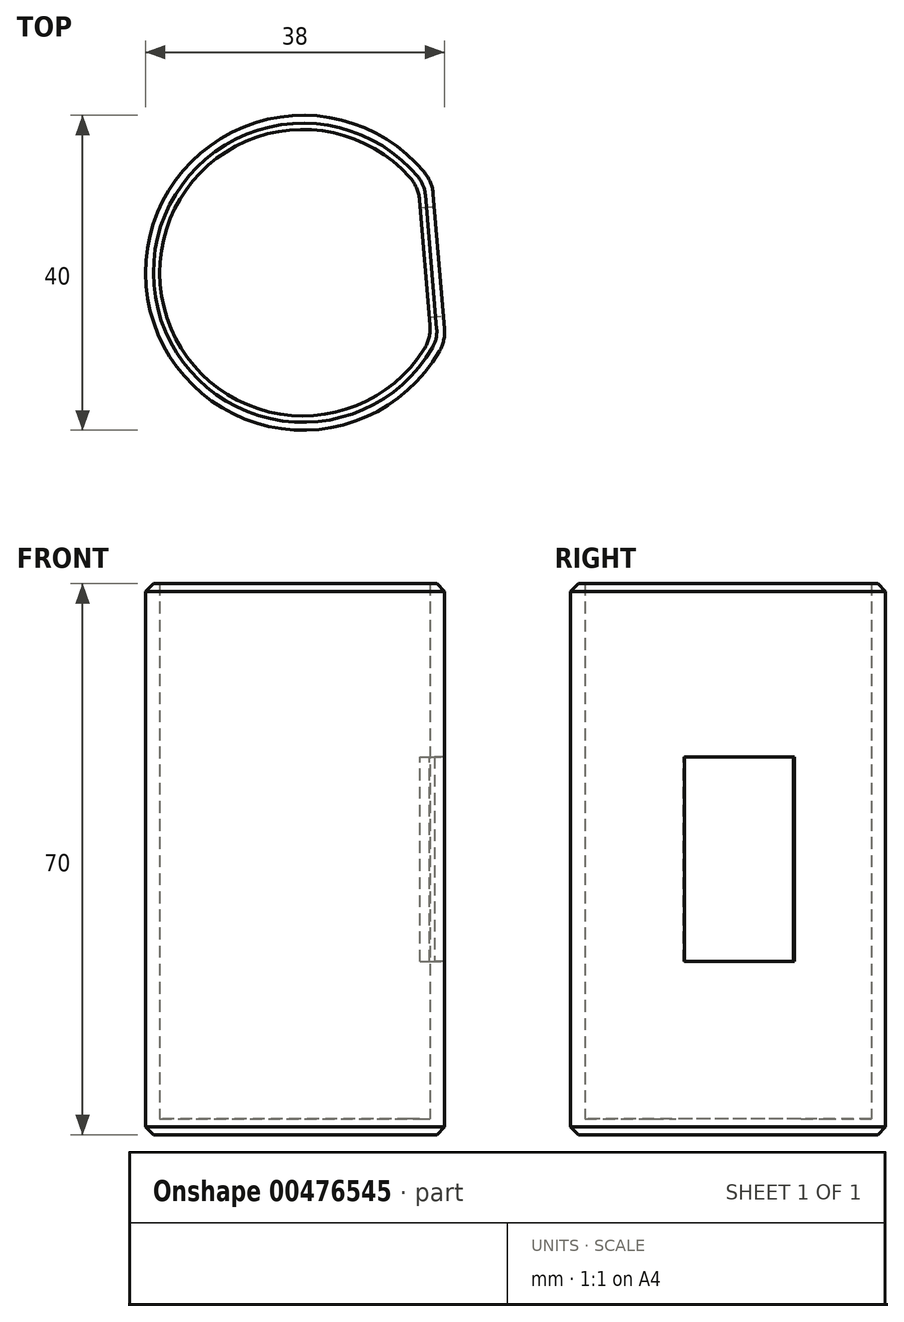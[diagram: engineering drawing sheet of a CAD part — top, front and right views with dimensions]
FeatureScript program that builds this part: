
annotation { "Feature Type Name" : "Feature", "Feature Type Description" : "" }
export const myFeature = defineFeature(function(context is Context, id is Id, definition is map)
    precondition{}
    {
        {
            var Q0;
            Q0=qCreatedBy(makeId("Top.planeOp"),FACE);
            var sketch = newSketch(context, id + "F0", { "sketchPlane" : qUnion([Q0])});
            skArc(sketch, "E0", {"start": v(16.42, 11.42) * mm, "mid": v(-19.93, -1.68) * mm, "end": v(18.1, -8.5) * mm});
            skLineSegment(sketch, "E1", {"start": v(16.42, 11.42) * mm, "end": v(18.1, -8.5) * mm});
            skArc(sketch, "E2.0", {"start": v(14.67, 10.78) * mm, "mid": v(-18.14, -1.53) * mm, "end": v(16.26, -8.17) * mm});
            skLineSegment(sketch, "E3.0", {"start": v(14.67, 10.78) * mm, "end": v(16.26, -8.17) * mm});
            skSolve(sketch);
        }
        {
            var Q0;
            Q0=makeQuery(id+"F0.imprint","IMPRINT",FACE,{"disambiguationData":[TD([[makeQuery(id+"F0.imprint","IMPRINT",EDGE,{"derivedFrom":sQuery(id+"F0.wireOp",EDGE,"E0")}),1.0]])]});
            extrude(context, id + "F1", {"entities" : qUnion([Q0]), "depth" : 70 * mm});
        }
        {
            var Q0;
            Q0=makeQuery(id+"F0.imprint","IMPRINT",FACE,{"disambiguationData":[TD([[makeQuery(id+"F0.imprint","IMPRINT",EDGE,{"derivedFrom":sQuery(id+"F0.wireOp",EDGE,"E2.0")}),1.0]])]});
            extrude(context, id + "F2", {"entities" : qUnion([Q0]), "operationType" : NewBodyOperationType.ADD, "depth" : 2 * mm});
        }
        {
            var Q0;
            {var subQ0=sQuery(id+"F0.wireOp",EDGE,"E1");var subQ1=sQuery(id+"F0.wireOp",EDGE,"E0");Q0=makeQuery(id+"F1.opExtrude","SWEPT_EDGE",EDGE,{"disambiguationData":[OSD([subQ1,subQ0]),TDD([makeQuery(id+"F0.imprint","INTERSECT",VERTEX,{"disambiguationData":[OD(1.0)],"derivedFrom":[subQ1,subQ0]})])]});}
            var Q1;
            {var subQ0=sQuery(id+"F0.wireOp",EDGE,"E1");var subQ1=sQuery(id+"F0.wireOp",EDGE,"E0");Q1=makeQuery(id+"F1.opExtrude","SWEPT_EDGE",EDGE,{"disambiguationData":[OSD([subQ1,subQ0]),TDD([makeQuery(id+"F0.imprint","INTERSECT",VERTEX,{"disambiguationData":[OD(0.0)],"derivedFrom":[subQ1,subQ0]})])]});}
            var Q2;
            {var subQ0=sQuery(id+"F0.wireOp",EDGE,"E3.0");var subQ1=sQuery(id+"F0.wireOp",EDGE,"E2.0");Q2=makeQuery(id+"F1.opExtrude","SWEPT_EDGE",EDGE,{"disambiguationData":[OSD([subQ1,subQ0]),TDD([makeQuery(id+"F0.imprint","INTERSECT",VERTEX,{"disambiguationData":[OD(1.0)],"derivedFrom":[subQ1,subQ0]})])]});}
            var Q3;
            {var subQ0=sQuery(id+"F0.wireOp",EDGE,"E3.0");var subQ1=sQuery(id+"F0.wireOp",EDGE,"E2.0");Q3=makeQuery(id+"F1.opExtrude","SWEPT_EDGE",EDGE,{"disambiguationData":[OSD([subQ1,subQ0]),TDD([makeQuery(id+"F0.imprint","INTERSECT",VERTEX,{"disambiguationData":[OD(0.0)],"derivedFrom":[subQ1,subQ0]})])]});}
            fillet(context, id + "F3", {"entities" : qUnion([Q0, Q1, Q2, Q3]), "radius" : 5 * mm, "tangentPropagation" : true, "allowEdgeOverflow" : false});
        }
        {
            var Q0;
            {var subQ0=sQuery(id+"F0.wireOp",EDGE,"E3.0");var subQ1=sQuery(id+"F0.wireOp",EDGE,"E2.0");Q0=makeQuery(id+"F2.boolean.opBoolean","MERGE",FACE,{"derivedFrom":[makeQuery(id+"F1.opExtrude","CAP_FACE",FACE,{"disambiguationData":[OSD([sQuery(id+"F0.wireOp",EDGE,"E0"),sQuery(id+"F0.wireOp",EDGE,"E1"),subQ1,subQ0])],"isStart":true}),makeQuery(id+"F2.opExtrude","CAP_FACE",FACE,{"disambiguationData":[OSD([subQ1,subQ0])],"isStart":true})]});}
            var Q1;
            Q1=makeQuery(id+"F1.opExtrude","CAP_EDGE",EDGE,{"disambiguationData":[OSD([sQuery(id+"F0.wireOp",EDGE,"E0")])],"isStart":false});
            var Q2;
            Q2=makeQuery(id+"F1.opExtrude","CAP_EDGE",EDGE,{"disambiguationData":[OSD([sQuery(id+"F0.wireOp",EDGE,"E1")])],"isStart":false});
            chamfer(context, id + "F4", {"entities" : qUnion([Q0, Q1, Q2]), "width" : 1 * mm, "tangentPropagation" : true});
        }
        {
            var Q0;
            Q0=makeQuery(id+"F1.opExtrude","SWEPT_FACE",FACE,{"disambiguationData":[OSD([sQuery(id+"F0.wireOp",EDGE,"E1")])]});
            var sketch = newSketch(context, id + "F5", { "sketchPlane" : qUnion([Q0])});
            skLineSegment(sketch, "E4.0.0", {"start": v(8.56, 1) * mm, "end": v(8.56, 69) * mm});
            skLineSegment(sketch, "E4.0.1", {"start": v(8.56, 69) * mm, "end": v(-8.56, 69) * mm});
            skLineSegment(sketch, "E4.0.2", {"start": v(-8.56, 69) * mm, "end": v(-8.56, 1) * mm});
            skLineSegment(sketch, "E4.0.3", {"start": v(-8.56, 1) * mm, "end": v(8.56, 1) * mm});
            skLineSegment(sketch, "E5.bottom", {"start": v(-7, 48) * mm, "end": v(7, 48) * mm});
            skLineSegment(sketch, "E5.top", {"start": v(-7, 22) * mm, "end": v(7, 22) * mm});
            skLineSegment(sketch, "E5.left", {"start": v(-7, 48) * mm, "end": v(-7, 22) * mm});
            skLineSegment(sketch, "E5.right", {"start": v(7, 48) * mm, "end": v(7, 22) * mm});
            skPoint(sketch, "E6", {"position": v(0, 22) * mm});
            skPoint(sketch, "E7", {"position": v(0, 1) * mm});
            skPoint(sketch, "E8", {"position": v(8.56, 35) * mm});
            skPoint(sketch, "E9", {"position": v(7, 35) * mm});
            skSolve(sketch);
        }
        {
            var Q0;
            Q0=makeQuery(id+"F5.imprint","IMPRINT",FACE,{"disambiguationData":[TD([[makeQuery(id+"F5.imprint","IMPRINT",EDGE,{"derivedFrom":sQuery(id+"F5.wireOp",EDGE,"E5.bottom")}),-1.0]])]});
            extrude(context, id + "F6", {"entities" : qUnion([Q0]), "operationType" : NewBodyOperationType.REMOVE, "endBound" : BoundingType.UP_TO_NEXT, "oppositeDirection" : true, "depth" : 25 * mm});
        }
    });
